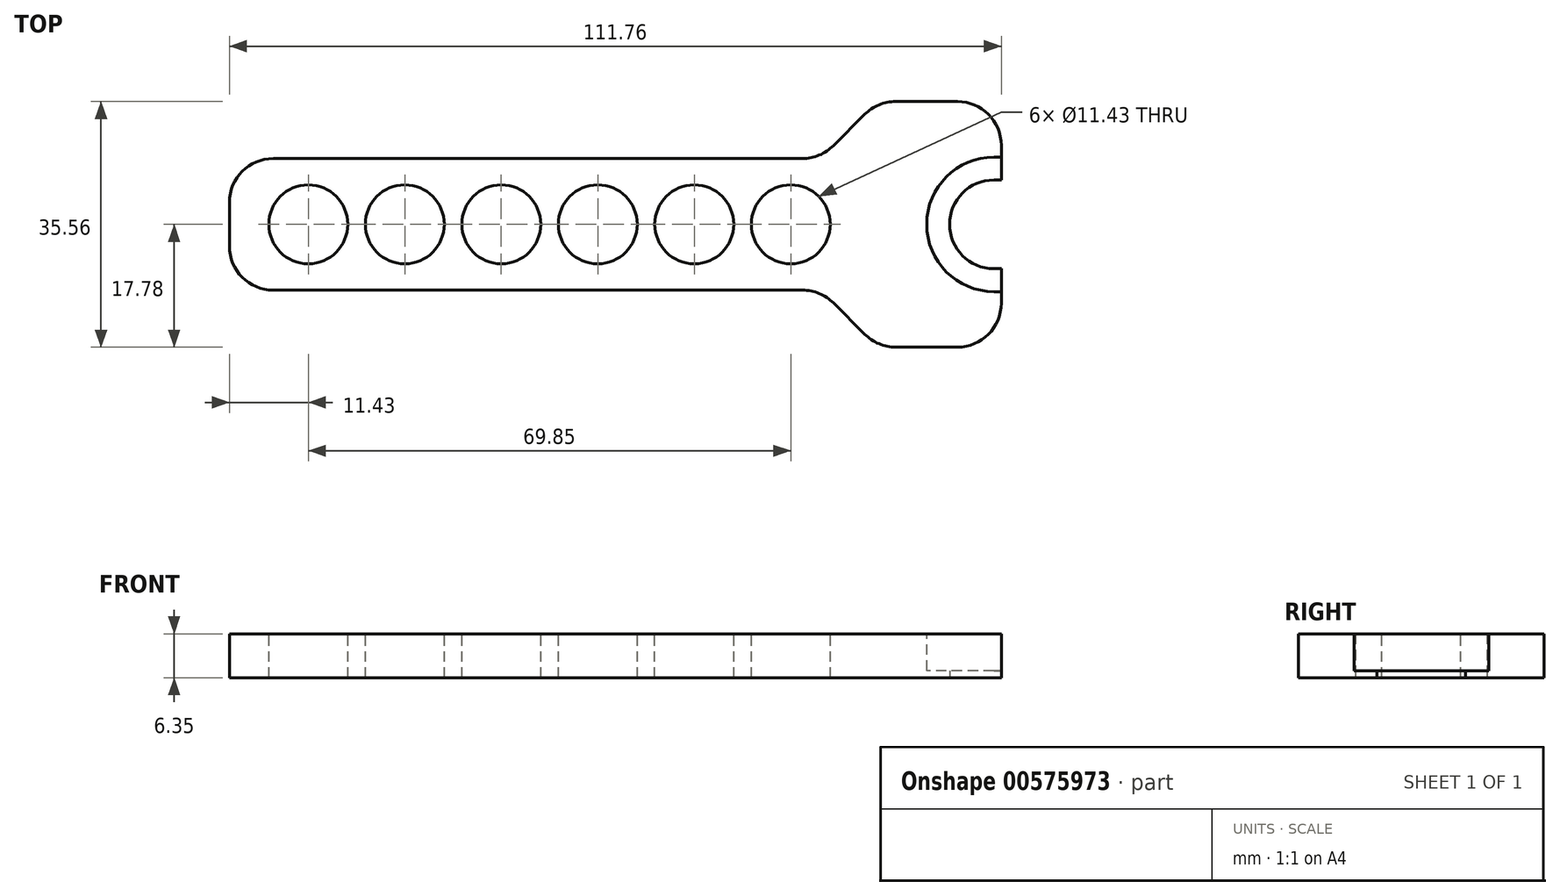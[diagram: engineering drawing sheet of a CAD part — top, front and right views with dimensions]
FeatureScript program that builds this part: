
annotation { "Feature Type Name" : "Feature", "Feature Type Description" : "" }
export const myFeature = defineFeature(function(context is Context, id is Id, definition is map)
    precondition{}
    {
        {
            var Q0;
            Q0=qCreatedBy(makeId("Top.planeOp"),FACE);
            var sketch = newSketch(context, id + "F0", { "sketchPlane" : qUnion([Q0])});
            skLineSegment(sketch, "E0.bottom", {"start": v(17.78, -17.78) * mm, "end": v(-17.78, -17.78) * mm});
            skLineSegment(sketch, "E0.top", {"start": v(17.78, 17.78) * mm, "end": v(-17.78, 17.78) * mm});
            skLineSegment(sketch, "E0.left", {"start": v(17.78, -17.78) * mm, "end": v(17.78, 17.78) * mm});
            skLineSegment(sketch, "E0.right", {"start": v(-17.78, -17.78) * mm, "end": v(-17.78, -9.53) * mm});
            skPoint(sketch, "E0.middle", {"position": v(0, 0) * mm});
            skArc(sketch, "E1", {"start": v(-8.14, -17.78) * mm, "mid": v(0, -23.06) * mm, "end": v(8.14, -17.78) * mm});
            skPoint(sketch, "E2.center.orphan", {"position": v(0, 15.65) * mm});
            skPoint(sketch, "E3.center.orphan", {"position": v(-13.58, 0) * mm});
            skPoint(sketch, "E4.center.orphan", {"position": v(13.88, 0) * mm});
            skLineSegment(sketch, "E5.bottom", {"start": v(-17.78, 9.53) * mm, "end": v(-93.98, 9.52) * mm});
            skLineSegment(sketch, "E5.top", {"start": v(-17.78, -9.53) * mm, "end": v(-93.98, -9.53) * mm});
            skLineSegment(sketch, "E5.right", {"start": v(-93.98, 9.52) * mm, "end": v(-93.98, -9.53) * mm});
            skLineSegment(sketch, "E6.trimOffspring", {"start": v(-17.78, 9.53) * mm, "end": v(-17.78, 17.78) * mm});
            skSolve(sketch);
        }
        {
            var Q0;
            Q0=makeQuery(id+"F0.imprint","IMPRINT",FACE,{"disambiguationData":[TD([[makeQuery(id+"F0.imprint","IMPRINT",EDGE,{"derivedFrom":sQuery(id+"F0.wireOp",EDGE,"E0.top")}),1.0]])]});
            extrude(context, id + "F1", {"entities" : qUnion([Q0]), "depth" : 6.35 * mm, "offsetDistance" : 25.4 * mm});
        }
        {
            var Q0;
            Q0=makeQuery(id+"F1.opExtrude","CAP_FACE",FACE,{"disambiguationData":[OSD([sQuery(id+"F0.wireOp",EDGE,"E0.bottom"),sQuery(id+"F0.wireOp",EDGE,"E0.top"),sQuery(id+"F0.wireOp",EDGE,"E0.left"),sQuery(id+"F0.wireOp",EDGE,"E0.right")])],"isStart":false});
            var sketch = newSketch(context, id + "F2", { "sketchPlane" : qUnion([Q0])});
            skArc(sketch, "E7", {"start": v(16.73, 9.74) * mm, "mid": v(6.99, 0) * mm, "end": v(16.73, -9.74) * mm});
            skLineSegment(sketch, "E8", {"start": v(16.73, 9.74) * mm, "end": v(17.78, 9.74) * mm});
            skLineSegment(sketch, "E9", {"start": v(16.73, -9.74) * mm, "end": v(17.78, -9.74) * mm});
            skPoint(sketch, "E10.orphan", {"position": v(-9.66, -17.78) * mm});
            skLineSegment(sketch, "E11", {"start": v(17.78, -9.74) * mm, "end": v(17.78, 9.74) * mm});
            skLineSegment(sketch, "E12", {"start": v(-9.72, -17.78) * mm, "end": v(-9.66, -17.78) * mm});
            skPoint(sketch, "E13.center.orphan", {"position": v(0, 16.7) * mm});
            skPoint(sketch, "E14.center.orphan", {"position": v(-16.7, 0) * mm});
            skPoint(sketch, "E15.end.orphan", {"position": v(-17.78, -9.72) * mm});
            skPoint(sketch, "E15.start.orphan", {"position": v(-17.78, 9.72) * mm});
            skPoint(sketch, "E16.center.orphan", {"position": v(0, -16.7) * mm});
            skPoint(sketch, "E17.end.orphan", {"position": v(9.72, -17.78) * mm});
            skSolve(sketch);
        }
        {
            var Q0;
            Q0=qSketchRegion(id+"F2",true);
            extrude(context, id + "F3", {"entities" : qUnion([Q0]), "operationType" : NewBodyOperationType.REMOVE, "oppositeDirection" : true, "depth" : 5.33 * mm, "offsetDistance" : 25.4 * mm});
        }
        {
            var Q0;
            Q0=makeQuery(id+"F1.opExtrude","CAP_FACE",FACE,{"disambiguationData":[OSD([sQuery(id+"F0.wireOp",EDGE,"E0.bottom"),sQuery(id+"F0.wireOp",EDGE,"E0.top"),sQuery(id+"F0.wireOp",EDGE,"E0.left"),sQuery(id+"F0.wireOp",EDGE,"E0.right")])],"isStart":true});
            var sketch = newSketch(context, id + "F4", { "sketchPlane" : qUnion([Q0])});
            skArc(sketch, "E18", {"start": v(16.7, 6.41) * mm, "mid": v(10.29, 0) * mm, "end": v(16.7, -6.41) * mm});
            skLineSegment(sketch, "E19", {"start": v(16.7, -6.41) * mm, "end": v(17.78, -6.41) * mm});
            skLineSegment(sketch, "E20", {"start": v(16.7, 6.41) * mm, "end": v(17.78, 6.41) * mm});
            skLineSegment(sketch, "E21", {"start": v(17.78, -6.41) * mm, "end": v(17.78, 6.41) * mm});
            skPoint(sketch, "E22.center.orphan", {"position": v(0, 16.32) * mm});
            skPoint(sketch, "E23.center.orphan", {"position": v(-16.45, 0) * mm});
            skPoint(sketch, "E24.start.orphan", {"position": v(-17.78, 6.41) * mm});
            skPoint(sketch, "E25.end.orphan", {"position": v(-17.78, -6.41) * mm});
            skPoint(sketch, "E26.center.orphan", {"position": v(0, -16.57) * mm});
            skPoint(sketch, "E27.start.orphan", {"position": v(-6.41, -17.78) * mm});
            skPoint(sketch, "E28.end.orphan", {"position": v(6.41, -17.78) * mm});
            skLineSegment(sketch, "E29.bottom", {"start": v(-17.78, -17.78) * mm, "end": v(0, -17.78) * mm});
            skLineSegment(sketch, "E29.top", {"start": v(-17.78, -9.53) * mm, "end": v(0, -9.53) * mm});
            skLineSegment(sketch, "E29.left", {"start": v(-17.78, -17.78) * mm, "end": v(-17.78, -9.53) * mm});
            skLineSegment(sketch, "E29.right", {"start": v(0, -17.78) * mm, "end": v(0, -9.53) * mm});
            skLineSegment(sketch, "E30.bottom", {"start": v(-17.78, 9.53) * mm, "end": v(0, 9.53) * mm});
            skLineSegment(sketch, "E30.top", {"start": v(-17.78, 17.78) * mm, "end": v(0, 17.78) * mm});
            skLineSegment(sketch, "E30.left", {"start": v(-17.78, 9.53) * mm, "end": v(-17.78, 17.78) * mm});
            skLineSegment(sketch, "E30.right", {"start": v(0, 9.53) * mm, "end": v(0, 17.78) * mm});
            skSolve(sketch);
        }
        {
            var Q0;
            Q0=qSketchRegion(id+"F4",true);
            extrude(context, id + "F5", {"entities" : qUnion([Q0]), "operationType" : NewBodyOperationType.REMOVE, "oppositeDirection" : true, "depth" : 25.4 * mm, "offsetDistance" : 25.4 * mm});
        }
        {
            var Q0;
            Q0=makeQuery(id+"F1.opExtrude","CAP_FACE",FACE,{"disambiguationData":[OSD([sQuery(id+"F0.wireOp",EDGE,"E0.bottom"),sQuery(id+"F0.wireOp",EDGE,"E0.top"),sQuery(id+"F0.wireOp",EDGE,"E0.left"),sQuery(id+"F0.wireOp",EDGE,"E0.right"),sQuery(id+"F0.wireOp",EDGE,"E5.bottom"),sQuery(id+"F0.wireOp",EDGE,"E5.top"),sQuery(id+"F0.wireOp",EDGE,"E5.right"),sQuery(id+"F0.wireOp",EDGE,"E6.trimOffspring")])],"isStart":false});
            var sketch = newSketch(context, id + "F6", { "sketchPlane" : qUnion([Q0])});
            skCircle(sketch, "E31", {"center": v(-82.55, 0) * mm, "radius": 5.72 * mm});
            skCircle(sketch, "E32", {"center": v(-68.58, 0) * mm, "radius": 5.72 * mm});
            skCircle(sketch, "E33", {"center": v(-54.6, 0) * mm, "radius": 5.72 * mm});
            skCircle(sketch, "E34", {"center": v(-40.64, 0) * mm, "radius": 5.72 * mm});
            skCircle(sketch, "E35", {"center": v(-26.67, 0) * mm, "radius": 5.72 * mm});
            skCircle(sketch, "E36", {"center": v(-12.7, 0) * mm, "radius": 5.72 * mm});
            skSolve(sketch);
        }
        {
            var Q0;
            Q0 = qSketchRegion(id + "F6", true);
            extrude(context, id + "F7", {"entities" : qUnion([Q0]), "operationType" : NewBodyOperationType.REMOVE, "oppositeDirection" : true, "depth" : 25.4 * mm, "offsetDistance" : 25.4 * mm});
        }
        {
            var Q0;
            Q0=makeQuery(id+"F5.boolean.opBoolean","COPY",EDGE,{"derivedFrom":makeQuery(id+"F5.opExtrude","SWEPT_EDGE",EDGE,{"disambiguationData":[OSD([sQuery(id+"F4.wireOp",EDGE,"E30.bottom"),sQuery(id+"F4.wireOp",EDGE,"E30.right")])]})});
            var Q1;
            Q1=makeQuery(id+"F5.boolean.opBoolean","COPY",EDGE,{"derivedFrom":makeQuery(id+"F5.opExtrude","SWEPT_EDGE",EDGE,{"disambiguationData":[OSD([sQuery(id+"F4.wireOp",EDGE,"E29.top"),sQuery(id+"F4.wireOp",EDGE,"E29.right")])]})});
            chamfer(context, id + "F8", {"entities" : qUnion([Q0, Q1]), "width" : 8.38 * mm, "tangentPropagation" : true});
        }
        {
            var Q0;
            {var subQ0=sQuery(id+"F4.wireOp",EDGE,"E30.bottom");Q0=makeQuery(id+"F8.opChamfer","BLEND_EDGE",EDGE,{"blendedFrom":[makeQuery(id+"F5.boolean.opBoolean","COPY",EDGE,{"derivedFrom":makeQuery(id+"F5.opExtrude","SWEPT_EDGE",EDGE,{"disambiguationData":[OSD([subQ0,sQuery(id+"F4.wireOp",EDGE,"E30.right")])]})}),makeQuery(id+"F5.boolean.opBoolean","MERGE",FACE,{"derivedFrom":[makeQuery(id+"F1.opExtrude","SWEPT_FACE",FACE,{"disambiguationData":[OSD([sQuery(id+"F0.wireOp",EDGE,"E5.top")])]})],"fromTools":[makeQuery(id+"F5.opExtrude","SWEPT_FACE",FACE,{"disambiguationData":[OSD([subQ0])]})]})],"blendedInto":[makeQuery(id+"F5.boolean.opBoolean","MERGE",FACE,{"derivedFrom":[makeQuery(id+"F1.opExtrude","SWEPT_FACE",FACE,{"disambiguationData":[OSD([sQuery(id+"F0.wireOp",EDGE,"E5.top")])]})],"fromTools":[makeQuery(id+"F5.opExtrude","SWEPT_FACE",FACE,{"disambiguationData":[OSD([subQ0])]})]})]});}
            var Q1;
            {var subQ0=sQuery(id+"F4.wireOp",EDGE,"E29.top");Q1=makeQuery(id+"F8.opChamfer","BLEND_EDGE",EDGE,{"blendedFrom":[makeQuery(id+"F5.boolean.opBoolean","COPY",EDGE,{"derivedFrom":makeQuery(id+"F5.opExtrude","SWEPT_EDGE",EDGE,{"disambiguationData":[OSD([subQ0,sQuery(id+"F4.wireOp",EDGE,"E29.right")])]})}),makeQuery(id+"F5.boolean.opBoolean","MERGE",FACE,{"derivedFrom":[makeQuery(id+"F1.opExtrude","SWEPT_FACE",FACE,{"disambiguationData":[OSD([sQuery(id+"F0.wireOp",EDGE,"E5.bottom")])]})],"fromTools":[makeQuery(id+"F5.opExtrude","SWEPT_FACE",FACE,{"disambiguationData":[OSD([subQ0])]})]})],"blendedInto":[makeQuery(id+"F5.boolean.opBoolean","MERGE",FACE,{"derivedFrom":[makeQuery(id+"F1.opExtrude","SWEPT_FACE",FACE,{"disambiguationData":[OSD([sQuery(id+"F0.wireOp",EDGE,"E5.bottom")])]})],"fromTools":[makeQuery(id+"F5.opExtrude","SWEPT_FACE",FACE,{"disambiguationData":[OSD([subQ0])]})]})]});}
            var Q2;
            Q2=makeQuery(id+"F8.opChamfer","BLEND_EDGE",EDGE,{"blendedFrom":[makeQuery(id+"F5.boolean.opBoolean","COPY",EDGE,{"derivedFrom":makeQuery(id+"F5.opExtrude","SWEPT_EDGE",EDGE,{"disambiguationData":[OSD([sQuery(id+"F4.wireOp",EDGE,"E29.top"),sQuery(id+"F4.wireOp",EDGE,"E29.right")])]})}),makeQuery(id+"F1.opExtrude","SWEPT_FACE",FACE,{"disambiguationData":[OSD([sQuery(id+"F0.wireOp",EDGE,"E0.top")])]})],"blendedInto":[makeQuery(id+"F1.opExtrude","SWEPT_FACE",FACE,{"disambiguationData":[OSD([sQuery(id+"F0.wireOp",EDGE,"E0.top")])]})]});
            var Q3;
            Q3=makeQuery(id+"F8.opChamfer","BLEND_EDGE",EDGE,{"blendedFrom":[makeQuery(id+"F5.boolean.opBoolean","COPY",EDGE,{"derivedFrom":makeQuery(id+"F5.opExtrude","SWEPT_EDGE",EDGE,{"disambiguationData":[OSD([sQuery(id+"F4.wireOp",EDGE,"E30.bottom"),sQuery(id+"F4.wireOp",EDGE,"E30.right")])]})}),makeQuery(id+"F1.opExtrude","SWEPT_FACE",FACE,{"disambiguationData":[OSD([sQuery(id+"F0.wireOp",EDGE,"E0.bottom")])]})],"blendedInto":[makeQuery(id+"F1.opExtrude","SWEPT_FACE",FACE,{"disambiguationData":[OSD([sQuery(id+"F0.wireOp",EDGE,"E0.bottom")])]})]});
            var Q4;
            Q4=makeQuery(id+"F1.opExtrude","SWEPT_EDGE",EDGE,{"disambiguationData":[OSD([sQuery(id+"F0.wireOp",EDGE,"E5.bottom"),sQuery(id+"F0.wireOp",EDGE,"E5.right")])]});
            var Q5;
            Q5=makeQuery(id+"F1.opExtrude","SWEPT_EDGE",EDGE,{"disambiguationData":[OSD([sQuery(id+"F0.wireOp",EDGE,"E5.top"),sQuery(id+"F0.wireOp",EDGE,"E5.right")])]});
            var Q6;
            Q6=makeQuery(id+"F1.opExtrude","SWEPT_EDGE",EDGE,{"disambiguationData":[OSD([sQuery(id+"F0.wireOp",EDGE,"E0.top"),sQuery(id+"F0.wireOp",EDGE,"E0.left")])]});
            var Q7;
            Q7=makeQuery(id+"F1.opExtrude","SWEPT_EDGE",EDGE,{"disambiguationData":[OSD([sQuery(id+"F0.wireOp",EDGE,"E0.bottom"),sQuery(id+"F0.wireOp",EDGE,"E0.left")])]});
            fillet(context, id + "F9", {"entities" : qUnion([Q0, Q1, Q2, Q3, Q4, Q5, Q6, Q7]), "tangentPropagation" : true, "radius" : 6.35 * mm, "defaultsChanged" : false, "vertexSettings" : [], "allowEdgeOverflow" : false});
        }
    });
